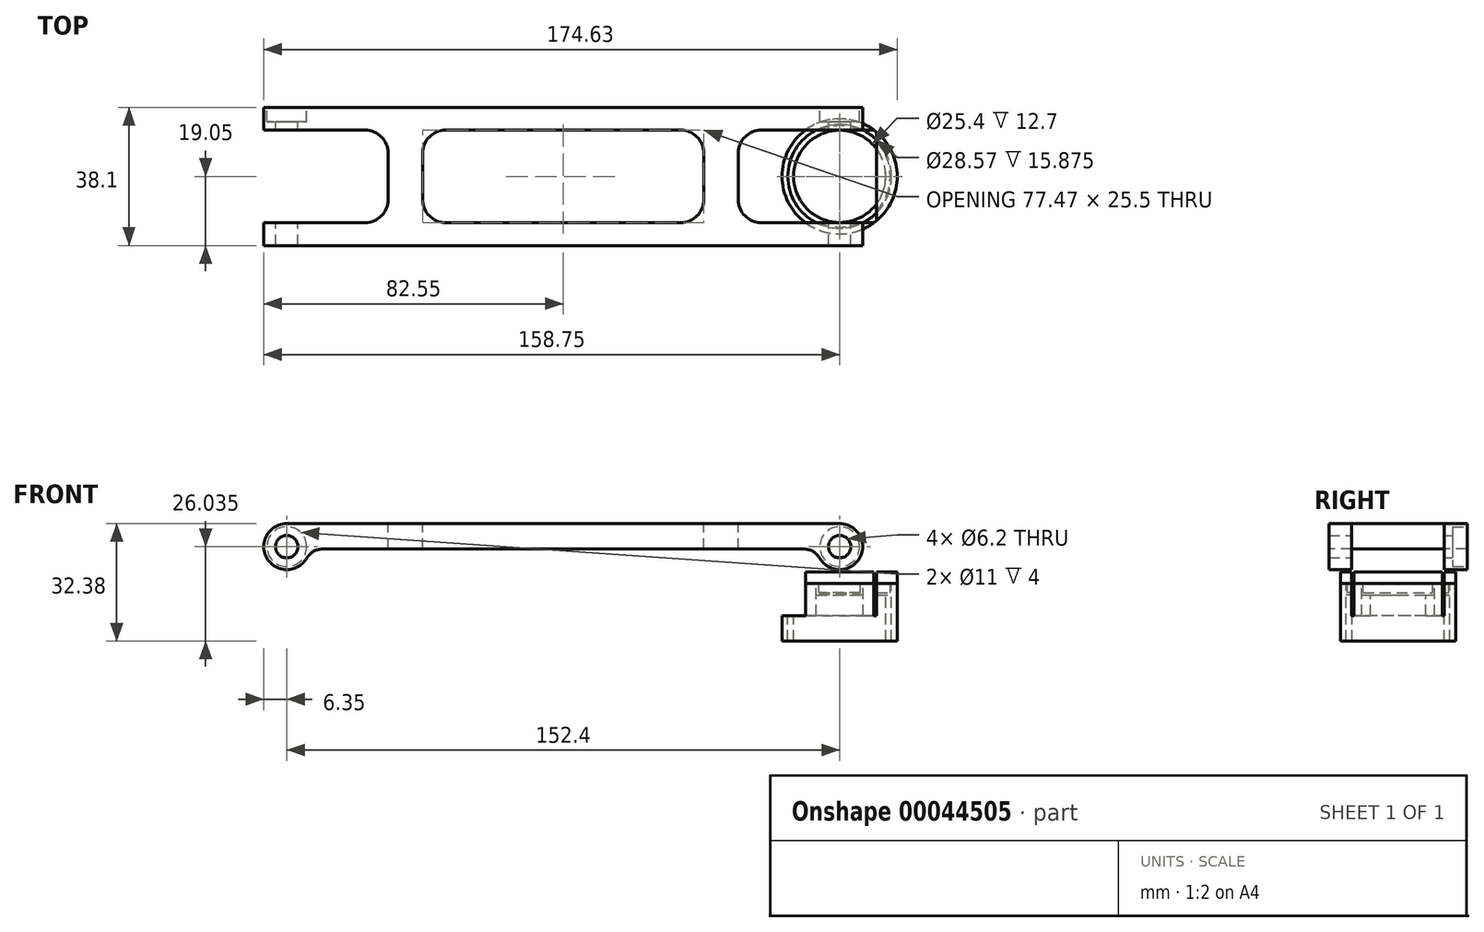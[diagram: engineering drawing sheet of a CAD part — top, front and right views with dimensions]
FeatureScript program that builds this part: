
annotation { "Feature Type Name" : "Feature", "Feature Type Description" : "" }
export const myFeature = defineFeature(function(context is Context, id is Id, definition is map)
    precondition{}
    {
        {
            var Q0;
            Q0=qCreatedBy(makeId("Right.planeOp"),FACE);
            var sketch = newSketch(context, id + "F0", { "sketchPlane" : qUnion([Q0])});
            skLineSegment(sketch, "E0", {"start": v(0, 48.36) * mm, "end": v(0, -51.46) * mm, "construction": true});
            skLineSegment(sketch, "E1.bottom", {"start": v(12.7, 0) * mm, "end": v(14.29, 0) * mm});
            skLineSegment(sketch, "E1.top", {"start": v(12.7, 12.7) * mm, "end": v(14.29, 12.7) * mm});
            skLineSegment(sketch, "E1.left", {"start": v(12.7, 0) * mm, "end": v(12.7, 12.7) * mm});
            skLineSegment(sketch, "E1.right", {"start": v(14.29, 0) * mm, "end": v(14.29, 12.7) * mm});
            skLineSegment(sketch, "E2.bottom", {"start": v(14.29, 0) * mm, "end": v(15.88, 0) * mm});
            skLineSegment(sketch, "E2.top", {"start": v(14.29, 15.88) * mm, "end": v(15.88, 15.88) * mm});
            skLineSegment(sketch, "E2.left", {"start": v(14.29, 0) * mm, "end": v(14.29, 15.88) * mm});
            skLineSegment(sketch, "E2.right", {"start": v(15.88, 0) * mm, "end": v(15.88, 15.88) * mm});
            skLineSegment(sketch, "E3", {"start": v(0, 13.33) * mm, "end": v(13.97, 13.33) * mm});
            skLineSegment(sketch, "E4", {"start": v(13.97, 13.33) * mm, "end": v(13.97, 15.88) * mm});
            skLineSegment(sketch, "E5", {"start": v(13.97, 15.88) * mm, "end": v(15.88, 15.88) * mm});
            skLineSegment(sketch, "E6", {"start": v(15.88, 15.88) * mm, "end": v(15.88, 19.05) * mm});
            skLineSegment(sketch, "E7", {"start": v(0, 13.33) * mm, "end": v(0, 19.05) * mm});
            skLineSegment(sketch, "E8", {"start": v(0, 19.05) * mm, "end": v(15.88, 19.05) * mm});
            skSolve(sketch);
        }
        {
            var Q0;
            Q0=makeQuery(id+"F0.imprint","IMPRINT",FACE,{"disambiguationData":[TD([[makeQuery(id+"F0.imprint","IMPRINT",EDGE,{"derivedFrom":sQuery(id+"F0.wireOp",EDGE,"E3")}),1.0]])]});
            var Q1;
            Q1=sQuery(id+"F0.wireOp",EDGE,"E0");
            revolve(context, id + "F1", {"entities" : qUnion([Q0]), "axis" : qUnion([Q1]), "revolveType" : RevolveType.FULL});
        }
        {
            var Q0;
            {var subQ2=sQuery(id+"F0.wireOp",EDGE,"E1.bottom");Q0=makeQuery(id+"F0.imprint","IMPRINT",FACE,{"disambiguationData":[TD([[makeQuery(id+"F0.imprint","IMPRINT",EDGE,{"derivedFrom":subQ2}),1.0]])]});}
            var Q1;
            Q1=sQuery(id+"F0.wireOp",EDGE,"E0");
            revolve(context, id + "F2", {"entities" : qUnion([Q0]), "axis" : qUnion([Q1]), "revolveType" : RevolveType.FULL});
        }
        {
            var Q0;
            {var subQ5=sQuery(id+"F0.wireOp",EDGE,"E2.bottom");Q0=makeQuery(id+"F0.imprint","IMPRINT",FACE,{"disambiguationData":[TD([[makeQuery(id+"F0.imprint","IMPRINT",EDGE,{"derivedFrom":subQ5}),1.0]])]});}
            var Q1;
            Q1=sQuery(id+"F0.wireOp",EDGE,"E0");
            revolve(context, id + "F3", {"entities" : qUnion([Q0]), "axis" : qUnion([Q1]), "revolveType" : RevolveType.FULL});
        }
        {
            var Q0;
            Q0=qCreatedBy(makeId("Front.planeOp"),FACE);
            var sketch = newSketch(context, id + "F4", { "sketchPlane" : qUnion([Q0])});
            skCircle(sketch, "E9", {"center": v(0, 26.04) * mm, "radius": 6.35 * mm});
            skCircle(sketch, "E10", {"center": v(0, 26.04) * mm, "radius": 3.1 * mm});
            skLineSegment(sketch, "E11", {"start": v(0, 32.39) * mm, "end": v(-152.4, 32.38) * mm});
            skCircle(sketch, "E12", {"center": v(-152.4, 26.03) * mm, "radius": 6.35 * mm});
            skCircle(sketch, "E13", {"center": v(-152.4, 26.03) * mm, "radius": 3.1 * mm});
            skLineSegment(sketch, "E14", {"start": v(5.92, 28.33) * mm, "end": v(9.53, 19.05) * mm});
            skLineSegment(sketch, "E15", {"start": v(9.53, 19.05) * mm, "end": v(-9.53, 19.05) * mm});
            skLineSegment(sketch, "E16", {"start": v(-9.53, 19.05) * mm, "end": v(-5.92, 28.33) * mm});
            skLineSegment(sketch, "E17", {"start": v(0, 26.04) * mm, "end": v(0, 19.05) * mm, "construction": true});
            skLineSegment(sketch, "E18", {"start": v(-146.08, 25.38) * mm, "end": v(-6.32, 25.39) * mm});
            skSolve(sketch);
        }
        {
            var Q0;
            Q0=makeQuery(id+"F4.imprint","IMPRINT",FACE,{"disambiguationData":[TD([[makeQuery(id+"F4.imprint","IMPRINT",EDGE,{"derivedFrom":sQuery(id+"F4.wireOp",EDGE,"E10")}),-1.0]])]});
            var Q1;
            {var subQ4=sQuery(id+"F4.wireOp",EDGE,"E14");Q1=makeQuery(id+"F4.imprint","IMPRINT",FACE,{"disambiguationData":[TD([[makeQuery(id+"F4.imprint","IMPRINT",EDGE,{"derivedFrom":subQ4}),-1.0]])]});}
            var Q2;
            {var subQ0=sQuery(id+"F4.wireOp",EDGE,"E16");Q2=makeQuery(id+"F4.imprint","IMPRINT",FACE,{"disambiguationData":[TD([[makeQuery(id+"F4.imprint","IMPRINT",EDGE,{"derivedFrom":subQ0}),-1.0]])]});}
            var Q3;
            {var subQ0=sQuery(id+"F4.wireOp",EDGE,"E18");var subQ3=sQuery(id+"F4.wireOp",EDGE,"E9");var subQ4=makeQuery(id+"F4.imprint","INTERSECT",VERTEX,{"derivedFrom":[subQ3,subQ0]});Q3=makeQuery(id+"F4.imprint","IMPRINT",FACE,{"disambiguationData":[TD([[makeQuery(id+"F4.imprint","IMPRINT",EDGE,{"disambiguationData":[TD([[subQ4,-1.0]])],"derivedFrom":subQ3}),-1.0]])]});}
            extrude(context, id + "F5", {"entities" : qUnion([Q0, Q1, Q2, Q3]), "operationType" : NewBodyOperationType.ADD, "endBound" : BoundingType.SYMMETRIC, "depth" : 25.4 * mm});
        }
        {
            var Q0;
            Q0=makeQuery(id+"F5.opExtrude","SWEPT_EDGE",EDGE,{"disambiguationData":[OSD([sQuery(id+"F4.wireOp",EDGE,"E14"),sQuery(id+"F4.wireOp",EDGE,"E15")])]});
            var Q1;
            Q1=makeQuery(id+"F5.opExtrude","SWEPT_EDGE",EDGE,{"disambiguationData":[OSD([sQuery(id+"F4.wireOp",EDGE,"E15"),sQuery(id+"F4.wireOp",EDGE,"E16")])]});
            fillet(context, id + "F6", {"entities" : qUnion([Q0, Q1]), "radius" : 6.35 * mm, "tangentPropagation" : true, "allowEdgeOverflow" : false});
        }
        {
            var Q0;
            Q0=makeQuery(id+"F6.opFillet","TWEAK_EDGE",EDGE,{"derivedFrom":[makeQuery(id+"F5.opExtrude","CAP_VERTEX",VERTEX,{"disambiguationData":[OSD([sQuery(id+"F4.wireOp",EDGE,"E15"),sQuery(id+"F4.wireOp",EDGE,"E16")])],"isStart":false})]});
            var Q1;
            Q1=makeQuery(id+"F6.opFillet","TWEAK_EDGE",EDGE,{"derivedFrom":[makeQuery(id+"F5.opExtrude","CAP_VERTEX",VERTEX,{"disambiguationData":[OSD([sQuery(id+"F4.wireOp",EDGE,"E14"),sQuery(id+"F4.wireOp",EDGE,"E15")])],"isStart":false})]});
            var Q2;
            Q2=makeQuery(id+"F6.opFillet","TWEAK_EDGE",EDGE,{"derivedFrom":[makeQuery(id+"F5.opExtrude","CAP_VERTEX",VERTEX,{"disambiguationData":[OSD([sQuery(id+"F4.wireOp",EDGE,"E14"),sQuery(id+"F4.wireOp",EDGE,"E15")])],"isStart":true})]});
            var Q3;
            Q3=makeQuery(id+"F6.opFillet","TWEAK_EDGE",EDGE,{"derivedFrom":[makeQuery(id+"F5.opExtrude","CAP_VERTEX",VERTEX,{"disambiguationData":[OSD([sQuery(id+"F4.wireOp",EDGE,"E15"),sQuery(id+"F4.wireOp",EDGE,"E16")])],"isStart":true})]});
            fillet(context, id + "F7", {"entities" : qUnion([Q0, Q1, Q2, Q3]), "radius" : 5.08 * mm, "tangentPropagation" : true, "allowEdgeOverflow" : false});
        }
        {
            var Q0;
            {var subQ1=sQuery(id+"F4.wireOp",EDGE,"E16");var subQ3=sQuery(id+"F4.wireOp",EDGE,"E9");var subQ5=makeQuery(id+"F4.imprint","INTERSECT",VERTEX,{"derivedFrom":[subQ3,subQ1]});Q0=makeQuery(id+"F4.imprint","IMPRINT",FACE,{"disambiguationData":[TD([[makeQuery(id+"F4.imprint","IMPRINT",EDGE,{"disambiguationData":[TD([[subQ5,-1.0]])],"derivedFrom":subQ3}),-1.0]])]});}
            var Q1;
            {var subQ7=sQuery(id+"F4.wireOp",EDGE,"E11");Q1=makeQuery(id+"F4.imprint","IMPRINT",FACE,{"disambiguationData":[TD([[makeQuery(id+"F4.imprint","IMPRINT",EDGE,{"derivedFrom":subQ7}),1.0]])]});}
            var Q2;
            Q2=makeQuery(id+"F4.imprint","IMPRINT",FACE,{"disambiguationData":[TD([[makeQuery(id+"F4.imprint","IMPRINT",EDGE,{"derivedFrom":sQuery(id+"F4.wireOp",EDGE,"E13")}),-1.0]])]});
            var Q3;
            Q3=makeQuery(id+"F4.imprint","IMPRINT",FACE,{"disambiguationData":[TD([[makeQuery(id+"F4.imprint","IMPRINT",EDGE,{"derivedFrom":sQuery(id+"F4.wireOp",EDGE,"E10")}),-1.0]])]});
            var Q4;
            {var subQ1=sQuery(id+"F4.wireOp",EDGE,"E16");var subQ3=sQuery(id+"F4.wireOp",EDGE,"E9");var subQ5=makeQuery(id+"F4.imprint","INTERSECT",VERTEX,{"derivedFrom":[subQ3,subQ1]});Q4=makeQuery(id+"F4.imprint","IMPRINT",FACE,{"disambiguationData":[TD([[makeQuery(id+"F4.imprint","IMPRINT",EDGE,{"disambiguationData":[TD([[subQ5,-1.0]])],"derivedFrom":subQ3}),-1.0]])]});}
            extrude(context, id + "F8", {"entities" : qUnion([Q0, Q1, Q2, Q3, Q4]), "endBound" : BoundingType.SYMMETRIC, "depth" : 38.1 * mm});
        }
        {
            var Q0;
            Q0=makeQuery(id+"F8.opExtrude","SWEPT_FACE",FACE,{"disambiguationData":[OSD([sQuery(id+"F4.wireOp",EDGE,"E11")])]});
            var sketch = newSketch(context, id + "F9", { "sketchPlane" : qUnion([Q0])});
            skLineSegment(sketch, "E19.bottom", {"start": v(10.16, -12.75) * mm, "end": v(-27.94, -12.75) * mm});
            skLineSegment(sketch, "E19.top", {"start": v(10.16, 12.75) * mm, "end": v(-27.94, 12.75) * mm});
            skLineSegment(sketch, "E19.left", {"start": v(10.16, -12.75) * mm, "end": v(10.16, 12.75) * mm});
            skLineSegment(sketch, "E19.right", {"start": v(-27.94, -12.75) * mm, "end": v(-27.94, 12.75) * mm});
            skLineSegment(sketch, "E20", {"start": v(-76.2, -19.05) * mm, "end": v(-76.2, 19.05) * mm, "construction": true});
            skLineSegment(sketch, "E21", {"start": v(0, 0) * mm, "end": v(-95.48, 0) * mm, "construction": true});
            skLineSegment(sketch, "E22", {"start": v(-76.2, -12.75) * mm, "end": v(-37.46, -12.75) * mm});
            skLineSegment(sketch, "E23", {"start": v(-37.46, -12.75) * mm, "end": v(-37.46, 12.75) * mm});
            skLineSegment(sketch, "E24", {"start": v(-37.46, 12.75) * mm, "end": v(-76.2, 12.75) * mm});
            skLineSegment(sketch, "E25.MirrorCS", {"start": v(-76.2, -12.75) * mm, "end": v(-114.94, -12.75) * mm});
            skLineSegment(sketch, "E26.MirrorCS", {"start": v(-114.94, -12.75) * mm, "end": v(-114.94, 12.75) * mm});
            skLineSegment(sketch, "E27.MirrorCS", {"start": v(-114.94, 12.75) * mm, "end": v(-76.2, 12.75) * mm});
            skLineSegment(sketch, "E28.MirrorCS", {"start": v(-124.46, -12.75) * mm, "end": v(-124.46, 12.75) * mm});
            skLineSegment(sketch, "E29.MirrorCS", {"start": v(-162.56, 12.75) * mm, "end": v(-124.46, 12.75) * mm});
            skLineSegment(sketch, "E30.MirrorCS", {"start": v(-162.56, -12.75) * mm, "end": v(-162.56, 12.75) * mm});
            skLineSegment(sketch, "E31.MirrorCS", {"start": v(-162.56, -12.75) * mm, "end": v(-124.46, -12.75) * mm});
            skSolve(sketch);
        }
        {
            var Q0;
            {var subQ5=sQuery(id+"F9.wireOp",EDGE,"E19.right");Q0=makeQuery(id+"F9.imprint","IMPRINT",FACE,{"disambiguationData":[TD([[makeQuery(id+"F9.imprint","IMPRINT",EDGE,{"derivedFrom":subQ5}),-1.0]])]});}
            var Q1;
            {var subQ5=sQuery(id+"F9.wireOp",EDGE,"E19.left");Q1=makeQuery(id+"F9.imprint","IMPRINT",FACE,{"disambiguationData":[TD([[makeQuery(id+"F9.imprint","IMPRINT",EDGE,{"derivedFrom":subQ5}),1.0]])]});}
            var Q2;
            Q2=makeQuery(id+"F9.imprint","IMPRINT",FACE,{"disambiguationData":[TD([[makeQuery(id+"F9.imprint","IMPRINT",EDGE,{"derivedFrom":sQuery(id+"F9.wireOp",EDGE,"E22")}),1.0]])]});
            var Q3;
            {var subQ5=sQuery(id+"F9.wireOp",EDGE,"E28.MirrorCS");Q3=makeQuery(id+"F9.imprint","IMPRINT",FACE,{"disambiguationData":[TD([[makeQuery(id+"F9.imprint","IMPRINT",EDGE,{"derivedFrom":subQ5}),1.0]])]});}
            var Q4;
            {var subQ5=sQuery(id+"F9.wireOp",EDGE,"E30.MirrorCS");Q4=makeQuery(id+"F9.imprint","IMPRINT",FACE,{"disambiguationData":[TD([[makeQuery(id+"F9.imprint","IMPRINT",EDGE,{"derivedFrom":subQ5}),-1.0]])]});}
            extrude(context, id + "F10", {"entities" : qUnion([Q0, Q1, Q2, Q3, Q4]), "operationType" : NewBodyOperationType.REMOVE, "oppositeDirection" : true, "depth" : 25.4 * mm});
        }
        {
            var Q0;
            Q0=makeQuery(id+"F10.boolean.opBoolean","COPY",EDGE,{"derivedFrom":makeQuery(id+"F10.opExtrude","SWEPT_EDGE",EDGE,{"disambiguationData":[OSD([sQuery(id+"F9.wireOp",EDGE,"E19.bottom"),sQuery(id+"F9.wireOp",EDGE,"E19.right")])]})});
            var Q1;
            Q1=makeQuery(id+"F10.boolean.opBoolean","COPY",EDGE,{"derivedFrom":makeQuery(id+"F10.opExtrude","SWEPT_EDGE",EDGE,{"disambiguationData":[OSD([sQuery(id+"F9.wireOp",EDGE,"E25.MirrorCS"),sQuery(id+"F9.wireOp",EDGE,"E26.MirrorCS")])]})});
            var Q2;
            Q2=makeQuery(id+"F10.boolean.opBoolean","COPY",EDGE,{"derivedFrom":makeQuery(id+"F10.opExtrude","SWEPT_EDGE",EDGE,{"disambiguationData":[OSD([sQuery(id+"F9.wireOp",EDGE,"E28.MirrorCS"),sQuery(id+"F9.wireOp",EDGE,"E29.MirrorCS")])]})});
            var Q3;
            Q3=makeQuery(id+"F10.boolean.opBoolean","COPY",EDGE,{"derivedFrom":makeQuery(id+"F10.opExtrude","SWEPT_EDGE",EDGE,{"disambiguationData":[OSD([sQuery(id+"F9.wireOp",EDGE,"E23"),sQuery(id+"F9.wireOp",EDGE,"E24")])]})});
            var Q4;
            Q4=makeQuery(id+"F10.boolean.opBoolean","COPY",EDGE,{"derivedFrom":makeQuery(id+"F10.opExtrude","SWEPT_EDGE",EDGE,{"disambiguationData":[OSD([sQuery(id+"F9.wireOp",EDGE,"E22"),sQuery(id+"F9.wireOp",EDGE,"E23")])]})});
            var Q5;
            Q5=makeQuery(id+"F10.boolean.opBoolean","COPY",EDGE,{"derivedFrom":makeQuery(id+"F10.opExtrude","SWEPT_EDGE",EDGE,{"disambiguationData":[OSD([sQuery(id+"F9.wireOp",EDGE,"E28.MirrorCS"),sQuery(id+"F9.wireOp",EDGE,"E31.MirrorCS")])]})});
            var Q6;
            Q6=makeQuery(id+"F10.boolean.opBoolean","COPY",EDGE,{"derivedFrom":makeQuery(id+"F10.opExtrude","SWEPT_EDGE",EDGE,{"disambiguationData":[OSD([sQuery(id+"F9.wireOp",EDGE,"E19.top"),sQuery(id+"F9.wireOp",EDGE,"E19.right")])]})});
            var Q7;
            Q7=makeQuery(id+"F10.boolean.opBoolean","COPY",EDGE,{"derivedFrom":makeQuery(id+"F10.opExtrude","SWEPT_EDGE",EDGE,{"disambiguationData":[OSD([sQuery(id+"F9.wireOp",EDGE,"E26.MirrorCS"),sQuery(id+"F9.wireOp",EDGE,"E27.MirrorCS")])]})});
            fillet(context, id + "F11", {"entities" : qUnion([Q0, Q1, Q2, Q3, Q4, Q5, Q6, Q7]), "radius" : 6.35 * mm, "tangentPropagation" : true, "allowEdgeOverflow" : false});
        }
        {
            var Q0;
            Q0=makeQuery(id+"F8.opExtrude","CAP_FACE",FACE,{"disambiguationData":[OSD([sQuery(id+"F4.wireOp",EDGE,"E9"),sQuery(id+"F4.wireOp",EDGE,"E10"),sQuery(id+"F4.wireOp",EDGE,"E11"),sQuery(id+"F4.wireOp",EDGE,"E12"),sQuery(id+"F4.wireOp",EDGE,"E13"),sQuery(id+"F4.wireOp",EDGE,"E18")])],"isStart":true});
            var sketch = newSketch(context, id + "F12", { "sketchPlane" : qUnion([Q0])});
            skPoint(sketch, "E32", {"position": v(0, 26.04) * mm});
            skPoint(sketch, "E33", {"position": v(152.4, 26.03) * mm});
            skSolve(sketch);
        }
        {
            var Q0;
            Q0=sQuery(id+"F12.wireOp",VERTEX,"E32");
            var Q1;
            Q1=sQuery(id+"F12.wireOp",VERTEX,"E33");
            var Q2;
            Q2=makeQuery(id+"F8.opExtrude","SWEPT_BODY",BODY,{"disambiguationData":[OSD([sQuery(id+"F4.wireOp",EDGE,"E9"),sQuery(id+"F4.wireOp",EDGE,"E10"),sQuery(id+"F4.wireOp",EDGE,"E11"),sQuery(id+"F4.wireOp",EDGE,"E12"),sQuery(id+"F4.wireOp",EDGE,"E13"),sQuery(id+"F4.wireOp",EDGE,"E18")])]});
            hole(context, id + "F13", {"style" : HoleStyle.C_BORE, "holeDiameter" : 6.2 * mm, "cBoreDiameter" : 11 * mm, "cBoreDepth" : 4 * mm, "endStyle" : HoleEndStyle.THROUGH, "locations" : qUnion([Q0, Q1]), "scope" : qUnion([Q2])});
        }
        {
            var Q0;
            Q0=qCreatedBy(makeId("Top.planeOp"),FACE);
            var Q1;
            Q1=sQuery(id+"F4.wireOp",VERTEX,"E11.start");
            cPlane(context, id + "F14", {"entities" : qUnion([Q0, Q1]), "cplaneType" : CPlaneType.PLANE_POINT, "offset" : 152.4 * mm, "width" : 152.4 * mm, "height" : 152.4 * mm});
        }
        {
            var Q0;
            Q0=qCreatedBy(id+"F14.planeOp",FACE);
            var sketch = newSketch(context, id + "F15", { "sketchPlane" : qUnion([Q0])});
            skPoint(sketch, "E34", {"position": v(0, 0) * mm});
            skSolve(sketch);
        }
        {
            var Q0;
            Q0=sQuery(id+"F15.wireOp",VERTEX,"E34");
            var Q1;
            Q1=makeQuery(id+"F1.opRevolve","SWEPT_BODY",BODY,{"disambiguationData":[OSD([sQuery(id+"F0.wireOp",EDGE,"E3"),sQuery(id+"F0.wireOp",EDGE,"E4"),sQuery(id+"F0.wireOp",EDGE,"E5"),sQuery(id+"F0.wireOp",EDGE,"E6"),sQuery(id+"F0.wireOp",EDGE,"E7"),sQuery(id+"F0.wireOp",EDGE,"d0dabe96-f203-41c9-a6db-38e8d674f194")])]});
            var Q2;
            Q2=makeQuery(id+"FiWZbtxw1kBBbdI_4.opExtrude","SWEPT_BODY",BODY,{"disambiguationData":[OSD([sQuery(id+"F4.wireOp",EDGE,"E10")])]});
            hole(context, id + "F16", {"style" : HoleStyle.C_BORE, "holeDiameter" : 6.2 * mm, "cBoreDiameter" : 10.2 * mm, "cBoreDepth" : 14 * mm, "endStyle" : HoleEndStyle.THROUGH, "locations" : qUnion([Q0]), "scope" : qUnion([Q1, Q2])});
        }
        {
            var Q0;
            {var subQ0=sQuery(id+"F4.wireOp",EDGE,"E12");var subQ1=sQuery(id+"F4.wireOp",EDGE,"E18");Q0=makeQuery(id+"F10.boolean.opBoolean","SPLIT",EDGE,{"disambiguationData":[TD([makeQuery(id+"F10.opExtrude","SWEPT_FACE",FACE,{"disambiguationData":[OSD([sQuery(id+"F9.wireOp",EDGE,"E31.MirrorCS")])]})])],"derivedFrom":makeQuery(id+"F8.opExtrude","SWEPT_EDGE",EDGE,{"disambiguationData":[OSD([subQ0,subQ1])]})});}
            var Q1;
            {var subQ0=sQuery(id+"F4.wireOp",EDGE,"E12");var subQ1=sQuery(id+"F4.wireOp",EDGE,"E18");Q1=makeQuery(id+"F10.boolean.opBoolean","SPLIT",EDGE,{"disambiguationData":[TD([makeQuery(id+"F10.opExtrude","SWEPT_FACE",FACE,{"disambiguationData":[OSD([sQuery(id+"F9.wireOp",EDGE,"E29.MirrorCS")])]})])],"derivedFrom":makeQuery(id+"F8.opExtrude","SWEPT_EDGE",EDGE,{"disambiguationData":[OSD([subQ0,subQ1])]})});}
            var Q2;
            {var subQ0=sQuery(id+"F4.wireOp",EDGE,"E9");var subQ1=sQuery(id+"F4.wireOp",EDGE,"E18");Q2=makeQuery(id+"F10.boolean.opBoolean","SPLIT",EDGE,{"disambiguationData":[TD([makeQuery(id+"F10.opExtrude","SWEPT_FACE",FACE,{"disambiguationData":[OSD([sQuery(id+"F9.wireOp",EDGE,"E19.bottom")])]})])],"derivedFrom":makeQuery(id+"F8.opExtrude","SWEPT_EDGE",EDGE,{"disambiguationData":[OSD([subQ0,subQ1])]})});}
            var Q3;
            {var subQ0=sQuery(id+"F4.wireOp",EDGE,"E9");var subQ1=sQuery(id+"F4.wireOp",EDGE,"E18");Q3=makeQuery(id+"F10.boolean.opBoolean","SPLIT",EDGE,{"disambiguationData":[TD([makeQuery(id+"F10.opExtrude","SWEPT_FACE",FACE,{"disambiguationData":[OSD([sQuery(id+"F9.wireOp",EDGE,"E19.top")])]})])],"derivedFrom":makeQuery(id+"F8.opExtrude","SWEPT_EDGE",EDGE,{"disambiguationData":[OSD([subQ0,subQ1])]})});}
            fillet(context, id + "F17", {"entities" : qUnion([Q0, Q1, Q2, Q3]), "radius" : 5 * mm, "tangentPropagation" : true, "allowEdgeOverflow" : false});
        }
    });
